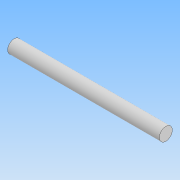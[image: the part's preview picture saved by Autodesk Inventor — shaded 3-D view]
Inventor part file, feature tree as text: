
AUTODESK INVENTOR PART (.ipt)
format: ipt  version: 2021 (Build 250183000, 183)  size: 73,216 bytes
history: native  units: mm
features: other x1, extrude x1, sketch x1
ambient origin geometry x8: Origin, YZ Plane, XZ Plane, XY Plane, X Axis, Y Axis, Z Axis, Center Point
bodies: Body1 (feature_tree)
feature tree (3):
  other  "實體1"
  extrude  "擠出1"  Depth=60.0mm
  sketch  "草圖1"
